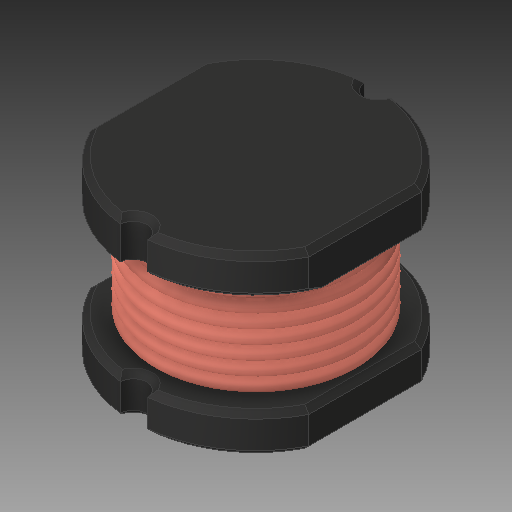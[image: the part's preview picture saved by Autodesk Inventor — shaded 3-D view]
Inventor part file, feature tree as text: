
AUTODESK INVENTOR PART (.ipt)
format: ipt  version: 2019 (Build 230136000, 136)  size: 425,984 bytes
history: mixed  units: in
note: dims shown in document units (in); Inventor stores cm internally (conversion verified against a paired STEP export)
features: helix x7, other x1, imported_body x1
ambient origin geometry x8: Origin, YZ Plane, XZ Plane, XY Plane, X Axis, Y Axis, Z Axis, Center Point
bodies: Solid1 (imported_parasolid), Solid2 (imported_parasolid), Solid3 (imported_parasolid), Solid4 (imported_parasolid), Solid5 (imported_parasolid), Solid6 (imported_parasolid), Solid7 (imported_parasolid), Solid8 (imported_parasolid)
feature tree (9):
  helix  "COIL"  [1 undecoded]
  helix  "COIL P[1]"  [1 undecoded]
  helix  "COIL P[2]"  [1 undecoded]
  helix  "COIL P[3]"  [1 undecoded]
  helix  "COIL P[4]"  [1 undecoded]
  helix  "COIL P[5]"  [1 undecoded]
  helix  "COIL P[6]"  [1 undecoded]
  other  "BASES C"
  imported_body  NMx_Import_Brep_tag  [imported B-rep: ~24 faces, bbox_mm=[1.750386, 3.0, 4.472222]]
note: 7 required parameter values undecoded (feature->parameter linkage not recoverable at this tier; creation-order binding heuristic only, values carry confidence <= 0.55)
